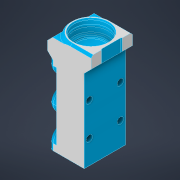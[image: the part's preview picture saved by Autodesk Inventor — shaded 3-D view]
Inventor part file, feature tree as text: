
AUTODESK INVENTOR PART (.ipt)
format: ipt  version: 2022.1 (Build 261234020, 234B)  size: 798,720 bytes
history: native  units: mm
features: sketch x18, other x12, chamfer x10, extrude x10, delete_face x8, fillet x8, projected_geometry x8, reference x7, plane x4, revolve x4, move_body x4, hole x3, direct_edit x3
ambient origin geometry x8: Origin, YZ Plane, XZ Plane, XY Plane, X Axis, Y Axis, Z Axis, Center Point
bodies: Volumenkörper1 (feature_tree)
feature tree (99):
  other  "Z-Joint_Base.iam"
  other  "Z-Joint_Base.ipt:1"
  other  "RBPB5.iam:1::RBPB5dummy.ipt:1"
  other  "RBPB5.iam:1::RBPB5h.ipt:1"
  other  "RBPB5.iam:1::RBPB5ball.ipt:1"
  delete_face  "Fläche löschen1"
  delete_face  "Fläche löschen2"
  plane  "Arbeitsebene1"
  revolve  "Umdrehung1"
  chamfer  "Fase1"  Distance=1.0mm Angle=45.0deg
  revolve  "Umdrehung2"
  sketch  "Skizze4"  dims[d3=0.14mm]
  plane  "Arbeitsebene2"
  extrude  "Extrusion1"  Depth=2.375mm
  extrude  "Extrusion3"  Depth=13.0mm
  chamfer  "Fase2"  Distance=31.0mm
  extrude  "Extrusion4"  Depth=0.4mm TaperAngle=0.0deg
  hole  "Bohrung1"  [1 undecoded]
  extrude  "Extrusion5"  Depth=1.8mm TaperAngle=0.0deg
  extrude  "Extrusion6"  Depth=6.5mm
  plane  "Arbeitsebene3"
  extrude  "Extrusion7"  TaperAngle=135.0deg  [1 undecoded]
  delete_face  "Fläche löschen3"
  revolve  "Umdrehung3"
  direct_edit  "Direktbearbeitung1"
  direct_edit  "Direktbearbeitung3"
  direct_edit  "Direktbearbeitung4"
  chamfer  "Fase7"  [1 undecoded]
  extrude  "Extrusion8"  Depth=4.0mm TaperAngle=0.0deg
  fillet  "Rundung4"  [1 undecoded]
  chamfer  "Fase9"  Distance=2.0mm
  fillet  "Rundung5"  Radius=2.0mm
  fillet  "Rundung6"  Radius=5.0mm
  fillet  "Rundung7"  Radius=2.0mm
  hole  "Bohrung2"  [1 undecoded]
  chamfer  "Fase10"  Distance=1.4mm
  extrude  "Extrusion9"  Depth=1.0mm
  chamfer  "Fase11"  Distance=0.6mm Angle=45.0deg
  fillet  "Rundung9"  Radius=5.0mm
  fillet  "Rundung10"  Radius=2.0mm
  delete_face  "Fläche löschen4"
  plane  "Arbeitsebene4"
  revolve  "Umdrehung4"
  fillet  "Rundung11"  Radius=20.0mm
  other  "Prägen1"
  hole  "Bohrung3"  [1 undecoded]
  chamfer  "Fase12"  Distance=7.5mm
  chamfer  "Fase13"  Angle=45.0deg  [1 undecoded]
  delete_face  "Fläche löschen5"
  delete_face  "Fläche löschen6"
  delete_face  "Fläche löschen7"
  extrude  "Extrusion10"  TaperAngle=135.0deg  [1 undecoded]
  extrude  "Extrusion11"  Depth=1.0mm
  chamfer  "Fase14"  [1 undecoded]
  delete_face  "Fläche löschen8"
  chamfer  "Fase15"  Distance=5.0mm
  fillet  "Rundung12"  Radius=2.0mm
  sketch  "Skizze1"  dims[d0=10.0mm]
  sketch  "Skizze3"  dims[d1=2.113333mm]
  projected_geometry  "Projizierte Kontur1"
  projected_geometry  "Projizierte Kontur2"
  sketch  "Skizze7"  dims[d4=90.0deg d5=1.0mm d6=0.5mm d7=45.0deg]
  sketch  "Skizze8"  dims[d9=11.112mm d10=2.375mm]
  reference  "Referenz5"
  reference  "Referenz6"
  projected_geometry  "Projizierte Kontur4"
  sketch  "Skizze9"  dims[d11=5.25mm d13=13.0mm]
  reference  "Referenz7"
  reference  "Referenz8"
  reference  "Referenz9"
  reference  "Referenz10"
  sketch  "Skizze10"  dims[d14=90.0deg d15=31.0mm d16=0.0mm]
  projected_geometry  "Projizierte Kontur5"
  sketch  "Skizze11"  dims[d19=9.2mm d20=0.4mm d21=0.0mm]
  projected_geometry  "Projizierte Kontur6"
  sketch  "Skizze12"  dims[d22=0.4mm d23=2.0mm d24=45.0deg d25=14.0mm]
  sketch  "Skizze13"  dims[d26=40.0mm d27=0.0mm]
  sketch  "Skizze14"  dims[d28=3.1mm d29=6.0mm d30=6.5mm d31=4.8mm d32=90.0deg d33=8.0mm d34=20.594885mm d35=1.8mm d36=0.0mm]
  sketch  "Skizze15"  dims[d43=6.5mm d44=6.5mm]
  reference  "Referenz11"
  sketch  "Skizze16"  dims[d45=1.8mm d46=0.0mm d47=135.0deg d48=0.0mm d49=0.0mm]
  projected_geometry  "Projizierte Kontur7"
  sketch  "Skizze17"  dims[d53=90.0deg d54=0.0mm d55=0.0mm d56=4.0mm]
  sketch  "Skizze18"  dims[d60=0.0mm d61=0.0mm d62=1.05mm]
  sketch  "Skizze19"  dims[d67=0.0mm d68=0.0mm d69=0.2mm]
  sketch  "Skizze20"  dims[d70=0.0mm d71=0.0mm d72=0.5mm]
  sketch  "Skizze21"  dims[d73=0.8mm d74=2.0mm d75=45.0deg d81=0.0mm d82=0.0mm d83=2.0mm d84=2.0mm d85=5.0mm d86=2.0mm d87=2.0mm d88=45.0deg d89=0.6mm d90=1.4mm d91=1.0mm d92=2.8mm d93=6.0mm d94=4.0mm d95=2.0mm d96=90.0deg d97=8.1mm d98=0.0mm d99=0.6mm d100=1.5mm d101=45.0deg d103=5.0mm d104=2.0mm d106=20.0mm d107=7.5mm d108=7.5mm d109=45.0deg d110=135.0deg d111=1.0mm d112=0.0mm d113=5.0mm d114=0.0mm d115=2.0mm d116=1.5mm d117=45.0deg d118=5.5mm d119=2.0mm d120=0.3mm d121=0.962857mm d122=0.15mm d123=0.15mm d124=0.9mm d125=1.775714mm d126=90.0deg d127=1.0mm d128=8.0mm d129=25.0mm d130=9.0mm d131=9.0mm d132=0.4mm d133=0.0mm d134=6.1mm d135=20.0mm d136=10.0mm d137=0.0mm d138=6.1mm d139=10.0mm d140=15.0mm d141=6.1mm d142=6.0mm d143=4.0mm d144=2.0mm d145=90.0deg d146=3.2mm d147=0.0mm d148=0.2mm d149=2.0mm d150=45.0deg d151=0.2mm d152=2.0mm d153=45.0deg d154=17.0mm d155=20.0mm d156=1.5mm d157=0.0mm d158=0.0mm d159=0.0mm d160=1.0mm d161=2.0mm d162=45.0deg d163=0.5mm d164=2.0mm d165=45.0deg d166=1.0mm d167=0.0mm d168=0.0mm d169=0.0mm d170=0.0mm]
  projected_geometry  "Projizierte Kontur9"
  projected_geometry  "Projizierte Kontur10"
  other  "Gruppe.iam"
  other  "<userpath>\Desktop\Voron-2-2.4r1\Custom\Misumi GE5C\Gruppe.iam"
  other  "MGN9H (1)_1:1"
  other  "MGN9H - Carriage:1"
  move_body  "Verschieben1"
  move_body  "Verschieben3"
  move_body  "Verschieben4"
  move_body  "Verschieben5"
  other  "Cover:1"
  other  "Schnittkanten projizieren1"
note: 9 required parameter values undecoded (feature->parameter linkage not recoverable at this tier; creation-order binding heuristic only, values carry confidence <= 0.55)
